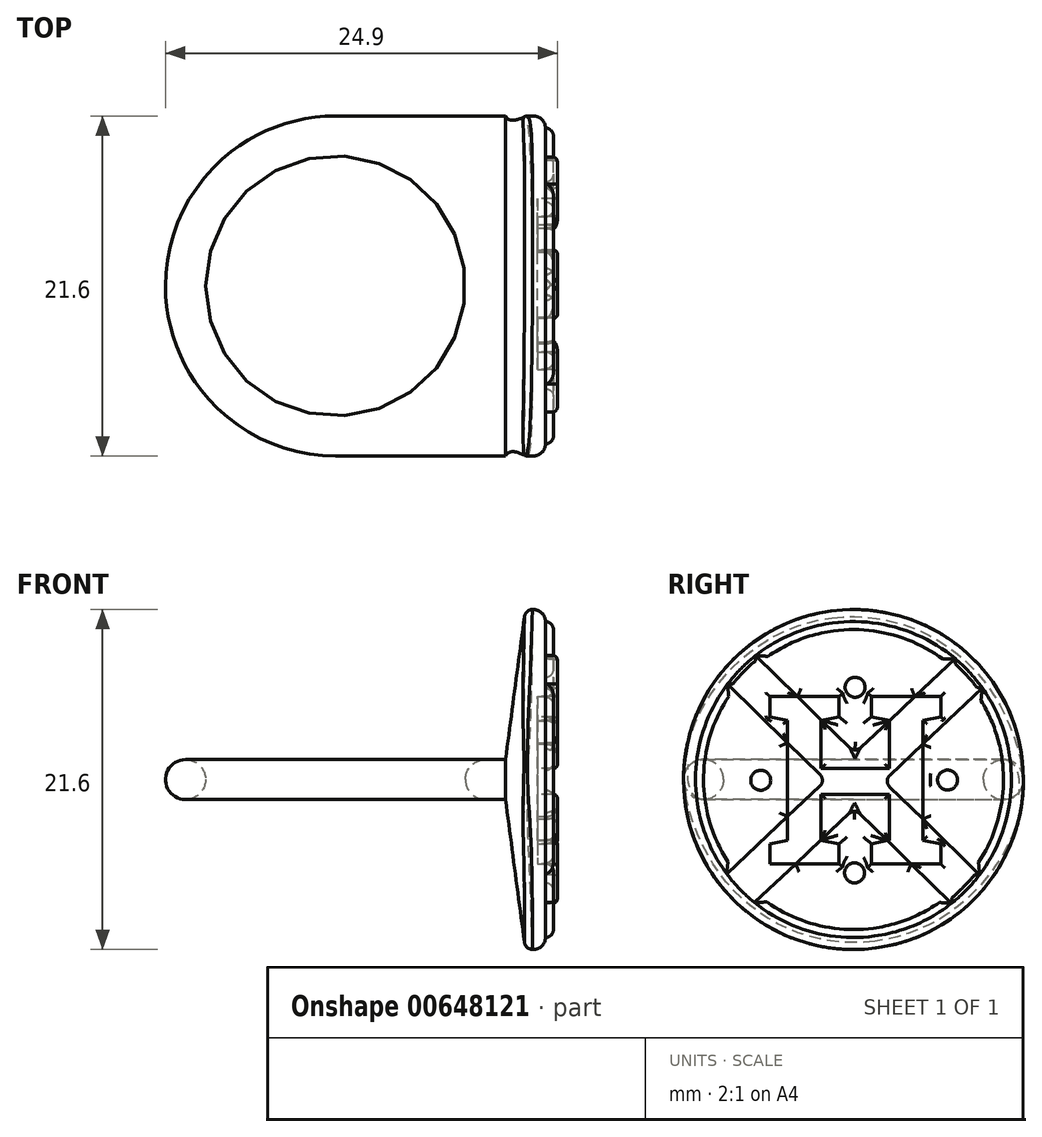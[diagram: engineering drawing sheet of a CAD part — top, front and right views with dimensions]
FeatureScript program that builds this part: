
annotation { "Feature Type Name" : "Feature", "Feature Type Description" : "" }
export const myFeature = defineFeature(function(context is Context, id is Id, definition is map)
    precondition{}
    {
        {
            var Q0;
            Q0=qCreatedBy(makeId("Top.planeOp"),FACE);
            var sketch = newSketch(context, id + "F0", { "sketchPlane" : qUnion([Q0])});
            skCircle(sketch, "E0", {"center": v(0, 0) * mm, "radius": 8.26 * mm});
            skCircle(sketch, "E1.0", {"center": v(0, 0) * mm, "radius": 10.8 * mm});
            skLineSegment(sketch, "E2", {"start": v(0, -10.8) * mm, "end": v(28.84, -10.8) * mm});
            skLineSegment(sketch, "E3", {"start": v(0, 10.8) * mm, "end": v(27.85, 10.8) * mm});
            skLineSegment(sketch, "E4", {"start": v(10.8, 0) * mm, "end": v(10.8, 10.8) * mm});
            skLineSegment(sketch, "E5", {"start": v(10.8, 10.8) * mm, "end": v(10.8, -10.8) * mm});
            skSolve(sketch);
        }
        {
            var Q0;
            Q0=qSketchRegion(id+"F0",true);
            extrude(context, id + "F1", {"entities" : qUnion([Q0]), "depth" : 2.54 * mm, "offsetDistance" : 25.4 * mm});
        }
        {
            var Q0;
            Q0=makeQuery(id+"F1.opExtrude","CAP_EDGE",EDGE,{"disambiguationData":[OSD([sQuery(id+"F0.wireOp",EDGE,"E0")])],"isStart":false});
            var Q1;
            Q1=makeQuery(id+"F1.opExtrude","CAP_EDGE",EDGE,{"disambiguationData":[OSD([sQuery(id+"F0.wireOp",EDGE,"E0")])],"isStart":true});
            var Q2;
            Q2=makeQuery(id+"F1.opExtrude","CAP_EDGE",EDGE,{"disambiguationData":[OSD([sQuery(id+"F0.wireOp",EDGE,"E1.0")])],"isStart":false});
            var Q3;
            Q3=makeQuery(id+"F1.opExtrude","CAP_EDGE",EDGE,{"disambiguationData":[OSD([sQuery(id+"F0.wireOp",EDGE,"E1.0")])],"isStart":true});
            fillet(context, id + "F2", {"entities" : qUnion([Q0, Q1, Q2, Q3]), "radius" : 1.27 * mm, "tangentPropagation" : true, "allowEdgeOverflow" : false});
        }
        {
            var Q0;
            Q0=makeQuery(id+"F1.opExtrude","SWEPT_FACE",FACE,{"disambiguationData":[OSD([sQuery(id+"F0.wireOp",EDGE,"E5")])]});
            cPlane(context, id + "F3", {"entities" : qUnion([Q0]), "cplaneType" : CPlaneType.OFFSET, "offset" : 1.27 * mm, "width" : 152.4 * mm, "height" : 152.4 * mm});
        }
        {
            var Q0;
            Q0=qCreatedBy(id+"F3.planeOp",FACE);
            var sketch = newSketch(context, id + "F4", { "sketchPlane" : qUnion([Q0])});
            skLineSegment(sketch, "E6", {"start": v(0, 0) * mm, "end": v(0, 2.54) * mm});
            skCircle(sketch, "E7", {"center": v(0, 1.27) * mm, "radius": 10.8 * mm});
            skSolve(sketch);
        }
        {
            var Q1;
            Q1=makeQuery(id+"F1.opExtrude","SWEPT_FACE",FACE,{"disambiguationData":[OSD([sQuery(id+"F0.wireOp",EDGE,"E5")])]});
            var Q2;
            Q2=makeQuery(id+"F4.imprint","IMPRINT",FACE,{"disambiguationData":[TD([[makeQuery(id+"F4.imprint","IMPRINT",EDGE,{"derivedFrom":sQuery(id+"F4.wireOp",EDGE,"E7")}),1.0]])]});
            loft(context, id + "F5", {"operationType" : NewBodyOperationType.ADD, "sheetProfilesArray" : [{ "sheetProfileEntities" : qUnion([Q1]) }, { "sheetProfileEntities" : qUnion([Q2]) }]});
        }
        {
            var Q0;
            Q0=makeQuery(id+"F5.opLoft","CAP_FACE",FACE,{"disambiguationData":[OSD([makeQuery(id+"F4.imprint","IMPRINT",FACE,{"disambiguationData":[TD([[makeQuery(id+"F4.imprint","IMPRINT",EDGE,{"derivedFrom":sQuery(id+"F4.wireOp",EDGE,"E7")}),1.0]])]})])],"isStart":true});
            extrude(context, id + "F6", {"entities" : qUnion([Q0]), "operationType" : NewBodyOperationType.ADD, "depth" : 1.27 * mm, "offsetDistance" : 25.4 * mm});
        }
        {
            var Q0;
            {var subQ0=sQuery(id+"F4.wireOp",EDGE,"E7");var subQ1=sQuery(id+"F0.wireOp",EDGE,"E5");var subQ2=makeQuery(id+"F1.opExtrude","SWEPT_FACE",FACE,{"disambiguationData":[OSD([subQ1])]});var subQ3=sQuery(id+"F0.wireOp",EDGE,"E3");var subQ4=sQuery(id+"F0.wireOp",EDGE,"E2");var subQ5=sQuery(id+"F0.wireOp",EDGE,"E1.0");var subQ6=sQuery(id+"F0.wireOp",EDGE,"E0");var subQ7=makeQuery(id+"F5.opLoft","MID_CAP_EDGE",EDGE,{"disambiguationData":[OSD([subQ6,subQ5,subQ4,subQ3,subQ1,subQ0]),TDD([makeQuery(id+"F2.opFillet","BLEND_VERTEX",VERTEX,{"blendedFrom":[makeQuery(id+"F1.opExtrude","CAP_EDGE",EDGE,{"disambiguationData":[OSD([subQ3])],"isStart":true}),makeQuery(id+"F1.opExtrude","CAP_FACE",FACE,{"disambiguationData":[OSD([subQ6,subQ5,subQ4,subQ3,subQ1])],"isStart":true}),subQ2],"blendedInto":[makeQuery(id+"F1.opExtrude","CAP_FACE",FACE,{"disambiguationData":[OSD([subQ6,subQ5,subQ4,subQ3,subQ1])],"isStart":true}),subQ2]}),makeQuery(id+"F2.opFillet","BLEND_VERTEX",VERTEX,{"blendedFrom":[makeQuery(id+"F1.opExtrude","CAP_EDGE",EDGE,{"disambiguationData":[OSD([subQ3])],"isStart":false}),makeQuery(id+"F1.opExtrude","CAP_FACE",FACE,{"disambiguationData":[OSD([subQ6,subQ5,subQ4,subQ3,subQ1])],"isStart":false}),subQ2],"blendedInto":[makeQuery(id+"F1.opExtrude","CAP_FACE",FACE,{"disambiguationData":[OSD([subQ6,subQ5,subQ4,subQ3,subQ1])],"isStart":false}),subQ2]}),makeQuery(id+"F4.imprint","IMPRINT",EDGE,{"derivedFrom":subQ0})])],"capPos":1.0});Q0=makeQuery(id+"F6.boolean.opBoolean","MERGE",EDGE,{"derivedFrom":[subQ7,makeQuery(id+"F6.opExtrude","CAP_EDGE",EDGE,{"disambiguationData":[OSD([subQ6,subQ5,subQ4,subQ3,subQ1,subQ0]),TDD([subQ7])],"isStart":true})]});}
            var Q1;
            {var subQ0=sQuery(id+"F4.wireOp",EDGE,"E7");var subQ1=sQuery(id+"F0.wireOp",EDGE,"E5");var subQ2=makeQuery(id+"F1.opExtrude","SWEPT_FACE",FACE,{"disambiguationData":[OSD([subQ1])]});var subQ3=sQuery(id+"F0.wireOp",EDGE,"E3");var subQ4=sQuery(id+"F0.wireOp",EDGE,"E2");var subQ5=sQuery(id+"F0.wireOp",EDGE,"E1.0");var subQ6=sQuery(id+"F0.wireOp",EDGE,"E0");var subQ7=makeQuery(id+"F1.opExtrude","CAP_FACE",FACE,{"disambiguationData":[OSD([subQ6,subQ5,subQ4,subQ3,subQ1])],"isStart":true});var subQ8=makeQuery(id+"F5.opLoft","MID_CAP_EDGE",EDGE,{"disambiguationData":[OSD([subQ6,subQ5,subQ4,subQ3,subQ1,subQ0]),TDD([makeQuery(id+"F2.opFillet","BLEND_VERTEX",VERTEX,{"blendedFrom":[makeQuery(id+"F1.opExtrude","CAP_EDGE",EDGE,{"disambiguationData":[OSD([subQ4])],"isStart":true}),subQ7,subQ2],"blendedInto":[subQ7,subQ2]}),makeQuery(id+"F2.opFillet","BLEND_VERTEX",VERTEX,{"blendedFrom":[makeQuery(id+"F1.opExtrude","CAP_EDGE",EDGE,{"disambiguationData":[OSD([subQ3])],"isStart":true}),subQ7,subQ2],"blendedInto":[subQ7,subQ2]}),makeQuery(id+"F4.imprint","IMPRINT",EDGE,{"derivedFrom":subQ0})])],"capPos":1.0});Q1=makeQuery(id+"F6.boolean.opBoolean","MERGE",EDGE,{"derivedFrom":[subQ8,makeQuery(id+"F6.opExtrude","CAP_EDGE",EDGE,{"disambiguationData":[OSD([subQ6,subQ5,subQ4,subQ3,subQ1,subQ0]),TDD([subQ8])],"isStart":true})]});}
            fillet(context, id + "F7", {"entities" : qUnion([Q0, Q1]), "radius" : 0.5 * mm, "tangentPropagation" : true, "allowEdgeOverflow" : false});
        }
        {
            var Q0;
            {var subQ0=sQuery(id+"F4.wireOp",EDGE,"E7");var subQ1=sQuery(id+"F0.wireOp",EDGE,"E5");var subQ2=makeQuery(id+"F1.opExtrude","SWEPT_FACE",FACE,{"disambiguationData":[OSD([subQ1])]});var subQ3=sQuery(id+"F0.wireOp",EDGE,"E3");var subQ4=sQuery(id+"F0.wireOp",EDGE,"E2");var subQ5=sQuery(id+"F0.wireOp",EDGE,"E1.0");var subQ6=sQuery(id+"F0.wireOp",EDGE,"E0");var subQ7=makeQuery(id+"F1.opExtrude","CAP_FACE",FACE,{"disambiguationData":[OSD([subQ6,subQ5,subQ4,subQ3,subQ1])],"isStart":true});Q0=makeQuery(id+"F6.opExtrude","CAP_EDGE",EDGE,{"disambiguationData":[OSD([subQ6,subQ5,subQ4,subQ3,subQ1,subQ0]),TDD([makeQuery(id+"F5.opLoft","MID_CAP_EDGE",EDGE,{"disambiguationData":[OSD([subQ6,subQ5,subQ4,subQ3,subQ1,subQ0]),TDD([makeQuery(id+"F2.opFillet","BLEND_VERTEX",VERTEX,{"blendedFrom":[makeQuery(id+"F1.opExtrude","CAP_EDGE",EDGE,{"disambiguationData":[OSD([subQ4])],"isStart":true}),subQ7,subQ2],"blendedInto":[subQ7,subQ2]}),makeQuery(id+"F2.opFillet","BLEND_VERTEX",VERTEX,{"blendedFrom":[makeQuery(id+"F1.opExtrude","CAP_EDGE",EDGE,{"disambiguationData":[OSD([subQ3])],"isStart":true}),subQ7,subQ2],"blendedInto":[subQ7,subQ2]}),makeQuery(id+"F4.imprint","IMPRINT",EDGE,{"derivedFrom":subQ0})])],"capPos":1.0})])],"isStart":false});}
            var Q1;
            {var subQ0=sQuery(id+"F4.wireOp",EDGE,"E7");var subQ1=sQuery(id+"F0.wireOp",EDGE,"E5");var subQ2=sQuery(id+"F0.wireOp",EDGE,"E3");var subQ3=sQuery(id+"F0.wireOp",EDGE,"E2");var subQ4=sQuery(id+"F0.wireOp",EDGE,"E1.0");var subQ5=sQuery(id+"F0.wireOp",EDGE,"E0");Q1=makeQuery(id+"F6.opExtrude","CAP_EDGE",EDGE,{"disambiguationData":[OSD([subQ5,subQ4,subQ3,subQ2,subQ1,subQ0]),TDD([makeQuery(id+"F5.opLoft","MID_CAP_EDGE",EDGE,{"disambiguationData":[OSD([subQ5,subQ4,subQ3,subQ2,subQ1,subQ0]),TDD([makeQuery(id+"F2.opFillet","BLEND_VERTEX",VERTEX,{"blendedFrom":[makeQuery(id+"F1.opExtrude","CAP_EDGE",EDGE,{"disambiguationData":[OSD([subQ3])],"isStart":true}),makeQuery(id+"F1.opExtrude","CAP_FACE",FACE,{"disambiguationData":[OSD([subQ5,subQ4,subQ3,subQ2,subQ1])],"isStart":true}),makeQuery(id+"F1.opExtrude","SWEPT_FACE",FACE,{"disambiguationData":[OSD([subQ1])]})],"blendedInto":[makeQuery(id+"F1.opExtrude","CAP_FACE",FACE,{"disambiguationData":[OSD([subQ5,subQ4,subQ3,subQ2,subQ1])],"isStart":true}),makeQuery(id+"F1.opExtrude","SWEPT_FACE",FACE,{"disambiguationData":[OSD([subQ1])]})]}),makeQuery(id+"F4.imprint","IMPRINT",EDGE,{"derivedFrom":subQ0})])],"capPos":1.0})])],"isStart":false});}
            fillet(context, id + "F8", {"entities" : qUnion([Q0, Q1]), "radius" : 0.76 * mm, "tangentPropagation" : true, "allowEdgeOverflow" : false});
        }
        {
            var Q0;
            Q0=makeQuery(id+"F6.opExtrude","CAP_FACE",FACE,{"disambiguationData":[OSD([makeQuery(id+"F4.imprint","IMPRINT",FACE,{"disambiguationData":[TD([[makeQuery(id+"F4.imprint","IMPRINT",EDGE,{"derivedFrom":sQuery(id+"F4.wireOp",EDGE,"E7")}),1.0]])]})])],"isStart":false});
            var sketch = newSketch(context, id + "F9", { "sketchPlane" : qUnion([Q0])});
            skLineSegment(sketch, "E8.0", {"start": v(-7.14, 6.5) * mm, "end": v(-1.75, 1.22) * mm});
            skLineSegment(sketch, "E9.0", {"start": v(-5.37, 8.31) * mm, "end": v(0.1, 2.96) * mm});
            skLineSegment(sketch, "E10.0", {"start": v(5.58, 8.12) * mm, "end": v(0.1, 2.96) * mm});
            skLineSegment(sketch, "E11.0", {"start": v(7.33, 6.27) * mm, "end": v(1.92, 1.18) * mm});
            skLineSegment(sketch, "E12.trimOffspring", {"start": v(-1.75, 1.22) * mm, "end": v(-7.17, -3.9) * mm});
            skLineSegment(sketch, "E13.trimOffspring", {"start": v(1.92, 1.18) * mm, "end": v(7.16, -3.95) * mm});
            skLineSegment(sketch, "E14.trimOffspring", {"start": v(0.07, -0.56) * mm, "end": v(-5.43, -5.74) * mm});
            skLineSegment(sketch, "E15.trimOffspring", {"start": v(0.07, -0.56) * mm, "end": v(5.38, -5.76) * mm});
            skLineSegment(sketch, "E16", {"start": v(7.16, -3.95) * mm, "end": v(8, -4.78) * mm});
            skLineSegment(sketch, "E17", {"start": v(8, -4.78) * mm, "end": v(1.92, 1.18) * mm});
            skLineSegment(sketch, "E18", {"start": v(6.23, -6.6) * mm, "end": v(5.38, -5.76) * mm});
            skLineSegment(sketch, "E19", {"start": v(-5.43, -5.74) * mm, "end": v(-6.29, -6.55) * mm});
            skLineSegment(sketch, "E20", {"start": v(-6.29, -6.55) * mm, "end": v(0.07, -0.56) * mm});
            skLineSegment(sketch, "E21", {"start": v(-7.17, -3.9) * mm, "end": v(-8.05, -4.72) * mm});
            skLineSegment(sketch, "E22", {"start": v(-8.05, -4.72) * mm, "end": v(-1.75, 1.22) * mm});
            skLineSegment(sketch, "E23.trimOffspring", {"start": v(0.1, 2.96) * mm, "end": v(6.46, 8.95) * mm});
            skLineSegment(sketch, "E24.trimOffspring", {"start": v(0.1, 2.96) * mm, "end": v(-6.22, 9.14) * mm});
            skLineSegment(sketch, "E25.trimOffspring", {"start": v(1.92, 1.18) * mm, "end": v(8.18, 7.08) * mm});
            skLineSegment(sketch, "E26.trimOffspring", {"start": v(-1.75, 1.22) * mm, "end": v(-8, 7.33) * mm});
            skLineSegment(sketch, "E27.trimOffspring", {"start": v(0.07, -0.56) * mm, "end": v(6.23, -6.6) * mm});
            skLineSegment(sketch, "E28", {"start": v(0.1, 2.96) * mm, "end": v(0.1, 11.3) * mm});
            skCircle(sketch, "E29", {"center": v(0.1, 7.13) * mm, "radius": 0.64 * mm});
            skLineSegment(sketch, "E30", {"start": v(1.92, 1.18) * mm, "end": v(10.03, 1.3) * mm});
            skPoint(sketch, "E30.endSnap0", {"position": v(4.75, 1.3) * mm});
            skCircle(sketch, "E31", {"center": v(5.98, 1.24) * mm, "radius": 0.64 * mm});
            skLineSegment(sketch, "E32", {"start": v(0.07, -0.56) * mm, "end": v(0.07, -8.76) * mm});
            skCircle(sketch, "E33", {"center": v(0.07, -4.66) * mm, "radius": 0.64 * mm});
            skLineSegment(sketch, "E34", {"start": v(-1.75, 1.22) * mm, "end": v(-10.03, 1.22) * mm});
            skCircle(sketch, "E35", {"center": v(-5.9, 1.22) * mm, "radius": 0.64 * mm});
            skText(sketch, "E36", { "text": "H", "fontName": "RobotoSlab-Bold.ttf"});
            const initialGuessF9  = {"E36": [-0.00572, -0.00408, 1, 0, 0.01075]};
            skSetInitialGuess(sketch, initialGuessF9);
            skSolve(sketch);
        }
        {
            var Q0;
            {var subQ0=sQuery(id+"F9.wireOp",EDGE,"E31");var subQ1=sQuery(id+"F9.wireOp",EDGE,"E30");var subQ2=makeQuery(id+"F9.imprint","INTERSECT",VERTEX,{"disambiguationData":[OD(0.0)],"derivedFrom":[subQ1,subQ0]});Q0=makeQuery(id+"F9.imprint","IMPRINT",FACE,{"disambiguationData":[TD([[makeQuery(id+"F9.imprint","IMPRINT",EDGE,{"disambiguationData":[TD([[subQ2,-1.0]])],"derivedFrom":subQ1}),1.0]])]});}
            var Q1;
            {var subQ0=sQuery(id+"F9.wireOp",EDGE,"E31");var subQ1=sQuery(id+"F9.wireOp",EDGE,"E30");var subQ2=makeQuery(id+"F9.imprint","INTERSECT",VERTEX,{"disambiguationData":[OD(0.0)],"derivedFrom":[subQ1,subQ0]});Q1=makeQuery(id+"F9.imprint","IMPRINT",FACE,{"disambiguationData":[TD([[makeQuery(id+"F9.imprint","IMPRINT",EDGE,{"disambiguationData":[TD([[subQ2,-1.0]])],"derivedFrom":subQ1}),-1.0]])]});}
            var Q2;
            {var subQ0=sQuery(id+"F9.wireOp",EDGE,"E33");var subQ1=sQuery(id+"F9.wireOp",EDGE,"E32");var subQ2=makeQuery(id+"F9.imprint","INTERSECT",VERTEX,{"disambiguationData":[OD(0.0)],"derivedFrom":[subQ1,subQ0]});Q2=makeQuery(id+"F9.imprint","IMPRINT",FACE,{"disambiguationData":[TD([[makeQuery(id+"F9.imprint","IMPRINT",EDGE,{"disambiguationData":[TD([[subQ2,-1.0]])],"derivedFrom":subQ1}),1.0]])]});}
            var Q3;
            {var subQ0=sQuery(id+"F9.wireOp",EDGE,"E33");var subQ1=sQuery(id+"F9.wireOp",EDGE,"E32");var subQ2=makeQuery(id+"F9.imprint","INTERSECT",VERTEX,{"disambiguationData":[OD(0.0)],"derivedFrom":[subQ1,subQ0]});Q3=makeQuery(id+"F9.imprint","IMPRINT",FACE,{"disambiguationData":[TD([[makeQuery(id+"F9.imprint","IMPRINT",EDGE,{"disambiguationData":[TD([[subQ2,-1.0]])],"derivedFrom":subQ1}),-1.0]])]});}
            var Q4;
            {var subQ0=sQuery(id+"F9.wireOp",EDGE,"E35");var subQ1=sQuery(id+"F9.wireOp",EDGE,"E34");var subQ2=makeQuery(id+"F9.imprint","INTERSECT",VERTEX,{"disambiguationData":[OD(0.0)],"derivedFrom":[subQ1,subQ0]});Q4=makeQuery(id+"F9.imprint","IMPRINT",FACE,{"disambiguationData":[TD([[makeQuery(id+"F9.imprint","IMPRINT",EDGE,{"disambiguationData":[TD([[subQ2,-1.0]])],"derivedFrom":subQ1}),-1.0]])]});}
            var Q5;
            {var subQ0=sQuery(id+"F9.wireOp",EDGE,"E35");var subQ1=sQuery(id+"F9.wireOp",EDGE,"E34");var subQ2=makeQuery(id+"F9.imprint","INTERSECT",VERTEX,{"disambiguationData":[OD(0.0)],"derivedFrom":[subQ1,subQ0]});Q5=makeQuery(id+"F9.imprint","IMPRINT",FACE,{"disambiguationData":[TD([[makeQuery(id+"F9.imprint","IMPRINT",EDGE,{"disambiguationData":[TD([[subQ2,-1.0]])],"derivedFrom":subQ1}),1.0]])]});}
            var Q6;
            {var subQ0=sQuery(id+"F9.wireOp",EDGE,"E29");var subQ1=sQuery(id+"F9.wireOp",EDGE,"E28");var subQ2=makeQuery(id+"F9.imprint","INTERSECT",VERTEX,{"disambiguationData":[OD(0.0)],"derivedFrom":[subQ1,subQ0]});Q6=makeQuery(id+"F9.imprint","IMPRINT",FACE,{"disambiguationData":[TD([[makeQuery(id+"F9.imprint","IMPRINT",EDGE,{"disambiguationData":[TD([[subQ2,-1.0]])],"derivedFrom":subQ1}),1.0]])]});}
            var Q7;
            {var subQ0=sQuery(id+"F9.wireOp",EDGE,"E29");var subQ1=sQuery(id+"F9.wireOp",EDGE,"E28");var subQ2=makeQuery(id+"F9.imprint","INTERSECT",VERTEX,{"disambiguationData":[OD(0.0)],"derivedFrom":[subQ1,subQ0]});Q7=makeQuery(id+"F9.imprint","IMPRINT",FACE,{"disambiguationData":[TD([[makeQuery(id+"F9.imprint","IMPRINT",EDGE,{"disambiguationData":[TD([[subQ2,-1.0]])],"derivedFrom":subQ1}),-1.0]])]});}
            extrude(context, id + "F10", {"entities" : qUnion([Q0, Q1, Q2, Q3, Q4, Q5, Q6, Q7]), "operationType" : NewBodyOperationType.ADD, "depth" : 0.5 * mm, "offsetDistance" : 25.4 * mm});
        }
        {
            var Q0;
            Q0=makeQuery(id+"F10.opExtrude","CAP_FACE",FACE,{"disambiguationData":[OSD([sQuery(id+"F9.wireOp",EDGE,"E29")])],"isStart":false});
            var Q1;
            Q1=makeQuery(id+"F10.opExtrude","CAP_FACE",FACE,{"disambiguationData":[OSD([sQuery(id+"F9.wireOp",EDGE,"E31")])],"isStart":false});
            var Q2;
            Q2=makeQuery(id+"F10.opExtrude","CAP_FACE",FACE,{"disambiguationData":[OSD([sQuery(id+"F9.wireOp",EDGE,"E33")])],"isStart":false});
            var Q3;
            Q3=makeQuery(id+"F10.opExtrude","CAP_FACE",FACE,{"disambiguationData":[OSD([sQuery(id+"F9.wireOp",EDGE,"E35")])],"isStart":false});
            fillet(context, id + "F11", {"entities" : qUnion([Q0, Q1, Q2, Q3]), "radius" : 0.5 * mm, "tangentPropagation" : true, "allowEdgeOverflow" : false});
        }
        {
            var Q0;
            {var subQ20=sQuery(id+"F9.wireOp",EDGE,"E36.sketch_text.stroke-0");Q0=makeQuery(id+"F9.imprint","IMPRINT",FACE,{"disambiguationData":[TD([[makeQuery(id+"F9.imprint","IMPRINT",EDGE,{"derivedFrom":subQ20}),1.0]])]});}
            var Q1;
            {var subQ0=sQuery(id+"F9.wireOp",EDGE,"E36.sketch_text.stroke-4");Q1=makeQuery(id+"F9.imprint","IMPRINT",FACE,{"disambiguationData":[TD([[makeQuery(id+"F9.imprint","IMPRINT",EDGE,{"derivedFrom":subQ0}),1.0]])]});}
            var Q2;
            {var subQ0=sQuery(id+"F9.wireOp",EDGE,"E36.sketch_text.stroke-21");Q2=makeQuery(id+"F9.imprint","IMPRINT",FACE,{"disambiguationData":[TD([[makeQuery(id+"F9.imprint","IMPRINT",EDGE,{"derivedFrom":subQ0}),1.0]])]});}
            var Q3;
            {var subQ5=sQuery(id+"F9.wireOp",EDGE,"E22");Q3=makeQuery(id+"F9.imprint","IMPRINT",FACE,{"disambiguationData":[TD([[makeQuery(id+"F9.imprint","IMPRINT",EDGE,{"derivedFrom":subQ5}),-1.0]])]});}
            var Q4;
            {var subQ0=sQuery(id+"F9.wireOp",EDGE,"E36.sketch_text.stroke-15");Q4=makeQuery(id+"F9.imprint","IMPRINT",FACE,{"disambiguationData":[TD([[makeQuery(id+"F9.imprint","IMPRINT",EDGE,{"derivedFrom":subQ0}),1.0]])]});}
            var Q5;
            {var subQ20=sQuery(id+"F9.wireOp",EDGE,"E36.sketch_text.stroke-11");Q5=makeQuery(id+"F9.imprint","IMPRINT",FACE,{"disambiguationData":[TD([[makeQuery(id+"F9.imprint","IMPRINT",EDGE,{"derivedFrom":subQ20}),1.0]])]});}
            extrude(context, id + "F12", {"entities" : qUnion([Q0, Q1, Q2, Q3, Q4, Q5]), "operationType" : NewBodyOperationType.ADD, "depth" : 0.76 * mm, "offsetDistance" : 25.4 * mm});
        }
        {
            var Q0;
            {var subQ37=sQuery(id+"F9.wireOp",EDGE,"E36.sketch_text.stroke-0");Q0=makeQuery(id+"F9.imprint","IMPRINT",FACE,{"disambiguationData":[TD([[makeQuery(id+"F9.imprint","IMPRINT",EDGE,{"derivedFrom":subQ37}),-1.0]])]});}
            extrude(context, id + "F13", {"entities" : qUnion([Q0]), "operationType" : NewBodyOperationType.REMOVE, "oppositeDirection" : true, "depth" : 0.5 * mm, "offsetDistance" : 25.4 * mm});
        }
        {
            var Q0;
            {var subQ0=sQuery(id+"F4.wireOp",EDGE,"E7");Q0=makeQuery(id+"F12.opExtrude","CAP_FACE",FACE,{"disambiguationData":[OSD([sQuery(id+"F0.wireOp",EDGE,"E0"),sQuery(id+"F0.wireOp",EDGE,"E1.0"),sQuery(id+"F0.wireOp",EDGE,"E2"),sQuery(id+"F0.wireOp",EDGE,"E3"),sQuery(id+"F0.wireOp",EDGE,"E5"),subQ0,makeQuery(id+"F4.imprint","IMPRINT",FACE,{"disambiguationData":[TD([[makeQuery(id+"F4.imprint","IMPRINT",EDGE,{"derivedFrom":subQ0}),1.0]])]}),sQuery(id+"F9.wireOp",EDGE,"E20"),sQuery(id+"F9.wireOp",EDGE,"E22"),sQuery(id+"F9.wireOp",EDGE,"E12.trimOffspring"),sQuery(id+"F9.wireOp",EDGE,"E36.sketch_text.stroke-25"),sQuery(id+"F9.wireOp",EDGE,"E36.sketch_text.stroke-26"),sQuery(id+"F9.wireOp",EDGE,"E36.sketch_text.stroke-27"),sQuery(id+"F9.wireOp",EDGE,"E36.sketch_text.stroke-28")])],"isStart":false});}
            var Q1;
            {var subQ0=sQuery(id+"F4.wireOp",EDGE,"E7");Q1=makeQuery(id+"F12.opExtrude","CAP_FACE",FACE,{"disambiguationData":[OSD([sQuery(id+"F0.wireOp",EDGE,"E0"),sQuery(id+"F0.wireOp",EDGE,"E1.0"),sQuery(id+"F0.wireOp",EDGE,"E2"),sQuery(id+"F0.wireOp",EDGE,"E3"),sQuery(id+"F0.wireOp",EDGE,"E5"),subQ0,makeQuery(id+"F4.imprint","IMPRINT",FACE,{"disambiguationData":[TD([[makeQuery(id+"F4.imprint","IMPRINT",EDGE,{"derivedFrom":subQ0}),1.0]])]}),sQuery(id+"F9.wireOp",EDGE,"E24.trimOffspring"),sQuery(id+"F9.wireOp",EDGE,"E26.trimOffspring"),sQuery(id+"F9.wireOp",EDGE,"E36.sketch_text.stroke-0"),sQuery(id+"F9.wireOp",EDGE,"E36.sketch_text.stroke-1"),sQuery(id+"F9.wireOp",EDGE,"E36.sketch_text.stroke-28"),sQuery(id+"F9.wireOp",EDGE,"E36.sketch_text.stroke-29")])],"isStart":false});}
            var Q2;
            {var subQ0=sQuery(id+"F4.wireOp",EDGE,"E7");Q2=makeQuery(id+"F12.opExtrude","CAP_FACE",FACE,{"disambiguationData":[OSD([sQuery(id+"F0.wireOp",EDGE,"E0"),sQuery(id+"F0.wireOp",EDGE,"E1.0"),sQuery(id+"F0.wireOp",EDGE,"E2"),sQuery(id+"F0.wireOp",EDGE,"E3"),sQuery(id+"F0.wireOp",EDGE,"E5"),subQ0,makeQuery(id+"F4.imprint","IMPRINT",FACE,{"disambiguationData":[TD([[makeQuery(id+"F4.imprint","IMPRINT",EDGE,{"derivedFrom":subQ0}),1.0]])]}),sQuery(id+"F9.wireOp",EDGE,"E23.trimOffspring"),sQuery(id+"F9.wireOp",EDGE,"E25.trimOffspring"),sQuery(id+"F9.wireOp",EDGE,"E36.sketch_text.stroke-10"),sQuery(id+"F9.wireOp",EDGE,"E36.sketch_text.stroke-11"),sQuery(id+"F9.wireOp",EDGE,"E36.sketch_text.stroke-12"),sQuery(id+"F9.wireOp",EDGE,"E36.sketch_text.stroke-13"),sQuery(id+"F9.wireOp",EDGE,"E36.sketch_text.stroke-14")])],"isStart":false});}
            var Q3;
            {var subQ0=sQuery(id+"F4.wireOp",EDGE,"E7");Q3=makeQuery(id+"F12.opExtrude","CAP_FACE",FACE,{"disambiguationData":[OSD([sQuery(id+"F0.wireOp",EDGE,"E0"),sQuery(id+"F0.wireOp",EDGE,"E1.0"),sQuery(id+"F0.wireOp",EDGE,"E2"),sQuery(id+"F0.wireOp",EDGE,"E3"),sQuery(id+"F0.wireOp",EDGE,"E5"),subQ0,makeQuery(id+"F4.imprint","IMPRINT",FACE,{"disambiguationData":[TD([[makeQuery(id+"F4.imprint","IMPRINT",EDGE,{"derivedFrom":subQ0}),1.0]])]}),sQuery(id+"F9.wireOp",EDGE,"E17"),sQuery(id+"F9.wireOp",EDGE,"E27.trimOffspring"),sQuery(id+"F9.wireOp",EDGE,"E36.sketch_text.stroke-14"),sQuery(id+"F9.wireOp",EDGE,"E36.sketch_text.stroke-15"),sQuery(id+"F9.wireOp",EDGE,"E36.sketch_text.stroke-16"),sQuery(id+"F9.wireOp",EDGE,"E36.sketch_text.stroke-17")])],"isStart":false});}
            var Q4;
            Q4=makeQuery(id+"F12.opExtrude","CAP_FACE",FACE,{"disambiguationData":[OSD([sQuery(id+"F9.wireOp",EDGE,"E20"),sQuery(id+"F9.wireOp",EDGE,"E27.trimOffspring"),sQuery(id+"F9.wireOp",EDGE,"E36.sketch_text.stroke-19"),sQuery(id+"F9.wireOp",EDGE,"E36.sketch_text.stroke-20"),sQuery(id+"F9.wireOp",EDGE,"E36.sketch_text.stroke-21"),sQuery(id+"F9.wireOp",EDGE,"E36.sketch_text.stroke-22")])],"isStart":false});
            var Q5;
            Q5=makeQuery(id+"F12.opExtrude","CAP_FACE",FACE,{"disambiguationData":[OSD([sQuery(id+"F9.wireOp",EDGE,"E23.trimOffspring"),sQuery(id+"F9.wireOp",EDGE,"E24.trimOffspring"),sQuery(id+"F9.wireOp",EDGE,"E36.sketch_text.stroke-3"),sQuery(id+"F9.wireOp",EDGE,"E36.sketch_text.stroke-4"),sQuery(id+"F9.wireOp",EDGE,"E36.sketch_text.stroke-5"),sQuery(id+"F9.wireOp",EDGE,"E36.sketch_text.stroke-6")])],"isStart":false});
            fillet(context, id + "F14", {"entities" : qUnion([Q0, Q1, Q2, Q3, Q4, Q5]), "radius" : 0.25 * mm, "tangentPropagation" : true, "allowEdgeOverflow" : false});
        }
        {
            var Q0;
            Q0=makeQuery(id+"F13.boolean.opBoolean","COPY",EDGE,{"derivedFrom":makeQuery(id+"F13.opExtrude","SWEPT_EDGE",EDGE,{"disambiguationData":[OSD([sQuery(id+"F9.wireOp",EDGE,"E26.trimOffspring"),sQuery(id+"F9.wireOp",EDGE,"E12.trimOffspring"),sQuery(id+"F9.wireOp",EDGE,"E34")])]})});
            var Q1;
            Q1=makeQuery(id+"F13.boolean.opBoolean","COPY",EDGE,{"derivedFrom":makeQuery(id+"F13.opExtrude","SWEPT_EDGE",EDGE,{"disambiguationData":[OSD([sQuery(id+"F9.wireOp",EDGE,"E17"),sQuery(id+"F9.wireOp",EDGE,"E25.trimOffspring"),sQuery(id+"F9.wireOp",EDGE,"E30")])]})});
            var Q2;
            Q2=makeQuery(id+"F12.opExtrude","SWEPT_EDGE",EDGE,{"disambiguationData":[OSD([sQuery(id+"F9.wireOp",EDGE,"E20"),sQuery(id+"F9.wireOp",EDGE,"E27.trimOffspring"),sQuery(id+"F9.wireOp",EDGE,"E32")])]});
            var Q3;
            Q3=makeQuery(id+"F12.opExtrude","SWEPT_EDGE",EDGE,{"disambiguationData":[OSD([sQuery(id+"F9.wireOp",EDGE,"E23.trimOffspring"),sQuery(id+"F9.wireOp",EDGE,"E24.trimOffspring"),sQuery(id+"F9.wireOp",EDGE,"E28")])]});
            fillet(context, id + "F15", {"entities" : qUnion([Q0, Q1, Q2, Q3]), "radius" : 0.5 * mm, "tangentPropagation" : true, "allowEdgeOverflow" : false});
        }
    });
